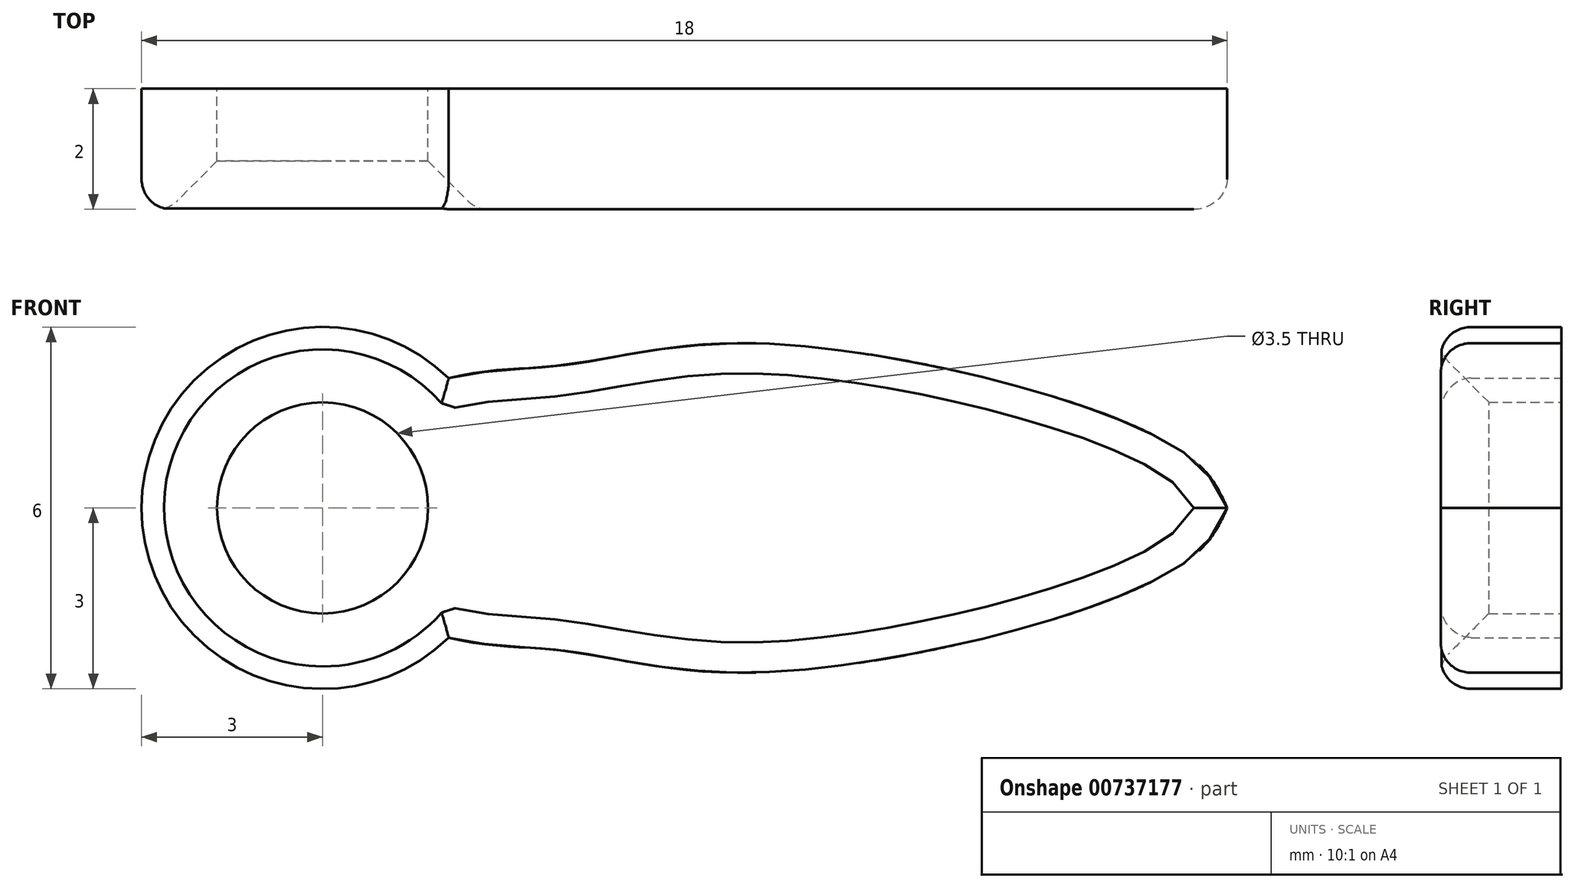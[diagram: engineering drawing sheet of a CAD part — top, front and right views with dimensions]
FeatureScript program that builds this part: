
annotation { "Feature Type Name" : "Feature", "Feature Type Description" : "" }
export const myFeature = defineFeature(function(context is Context, id is Id, definition is map)
    precondition{}
    {
        {
            var Q0;
            Q0=qCreatedBy(makeId("Front.planeOp"),FACE);
            var sketch = newSketch(context, id + "F0", { "sketchPlane" : qUnion([Q0])});
            skCircle(sketch, "E0", {"center": v(0, 0) * mm, "radius": 1.75 * mm});
            skArc(sketch, "E1", {"start": v(2.1, 2.15) * mm, "mid": v(-3, 0) * mm, "end": v(2.1, -2.15) * mm});
            skPoint(sketch, "E2", {"position": v(15, 0) * mm});
            skFitSpline(sketch, "E3", {"points": [v(15, 0) * mm, v(14.61, 0.64) * mm, v(12.62, 1.68) * mm, v(6.87, 2.73) * mm, v(3.98, 2.36) * mm, v(2.1, 2.15) * mm], "startDerivative": vector(-2.64, 5.93) * mm, "endDerivative": vector(-11.77, -3.08) * mm});
            skFitSpline(sketch, "E4.MirrorCS", {"points": [v(15, 0) * mm, v(14.61, -0.64) * mm, v(12.62, -1.68) * mm, v(6.87, -2.73) * mm, v(3.98, -2.36) * mm, v(2.1, -2.15) * mm], "startDerivative": vector(-2.64, -5.93) * mm, "endDerivative": vector(-11.77, 3.08) * mm});
            skSolve(sketch);
        }
        {
            var Q0;
            Q0=makeQuery(id+"F0.imprint","IMPRINT",FACE,{"disambiguationData":[TD([[makeQuery(id+"F0.imprint","IMPRINT",EDGE,{"derivedFrom":sQuery(id+"F0.wireOp",EDGE,"E0")}),-1.0]])]});
            extrude(context, id + "F1", {"entities" : qUnion([Q0]), "depth" : 2 * mm, "offsetDistance" : 25 * mm});
        }
        {
            var Q0;
            Q0=makeQuery(id+"F1.opExtrude","CAP_EDGE",EDGE,{"disambiguationData":[OSD([sQuery(id+"F0.wireOp",EDGE,"E0")])],"isStart":false});
            chamfer(context, id + "F2", {"entities" : qUnion([Q0]), "width" : 0.8 * mm, "tangentPropagation" : true});
        }
        {
            var Q0;
            Q0=makeQuery(id+"F1.opExtrude","CAP_FACE",FACE,{"disambiguationData":[OSD([sQuery(id+"F0.wireOp",EDGE,"E0"),sQuery(id+"F0.wireOp",EDGE,"E1"),sQuery(id+"F0.wireOp",EDGE,"E3"),sQuery(id+"F0.wireOp",EDGE,"E4.MirrorCS")])],"isStart":false});
            fillet(context, id + "F3", {"entities" : qUnion([Q0]), "radius" : 0.5 * mm, "tangentPropagation" : true, "allowEdgeOverflow" : false});
        }
    });
